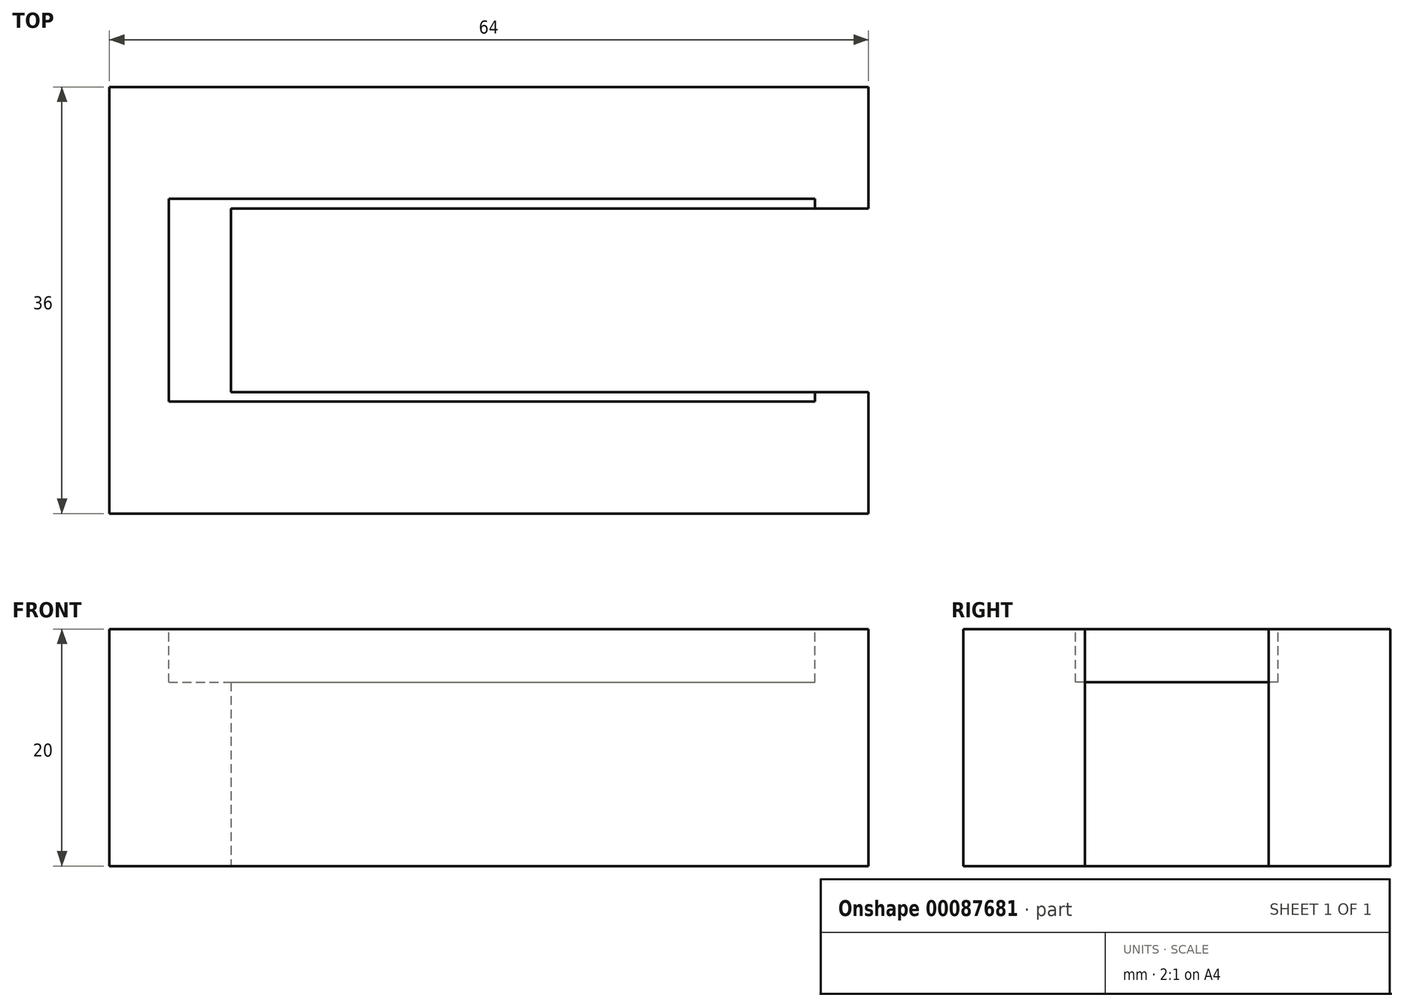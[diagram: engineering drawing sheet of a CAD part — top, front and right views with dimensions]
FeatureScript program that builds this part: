
annotation { "Feature Type Name" : "Feature", "Feature Type Description" : "" }
export const myFeature = defineFeature(function(context is Context, id is Id, definition is map)
    precondition{}
    {
        {
            var Q0;
            Q0=qCreatedBy(makeId("Top.planeOp"),FACE);
            var sketch = newSketch(context, id + "F0", { "sketchPlane" : qUnion([Q0])});
            skLineSegment(sketch, "E0", {"start": v(53.75, 0) * mm, "end": v(-10.25, 0) * mm});
            skLineSegment(sketch, "E1", {"start": v(-10.25, 0) * mm, "end": v(-10.25, 36) * mm});
            skLineSegment(sketch, "E2", {"start": v(-10.25, 36) * mm, "end": v(53.75, 36) * mm});
            skLineSegment(sketch, "E3", {"start": v(53.75, 36) * mm, "end": v(53.75, 25.75) * mm});
            skLineSegment(sketch, "E4", {"start": v(53.75, 25.75) * mm, "end": v(0, 25.75) * mm});
            skLineSegment(sketch, "E5", {"start": v(0, 25.75) * mm, "end": v(0, 10.25) * mm});
            skLineSegment(sketch, "E6", {"start": v(0, 10.25) * mm, "end": v(53.75, 10.25) * mm});
            skLineSegment(sketch, "E7", {"start": v(53.75, 10.25) * mm, "end": v(53.75, 0) * mm});
            skSolve(sketch);
        }
        {
            var Q0;
            Q0=makeQuery(id+"F0.imprint","IMPRINT",FACE,{"disambiguationData":[TD([[makeQuery(id+"F0.imprint","IMPRINT",EDGE,{"derivedFrom":sQuery(id+"F0.wireOp",EDGE,"E0")}),-1.0]])]});
            extrude(context, id + "F1", {"entities" : qUnion([Q0]), "depth" : 20 * mm});
        }
        {
            var Q0;
            Q0=makeQuery(id+"F1.opExtrude","CAP_FACE",FACE,{"disambiguationData":[OSD([sQuery(id+"F0.wireOp",EDGE,"E0"),sQuery(id+"F0.wireOp",EDGE,"E1"),sQuery(id+"F0.wireOp",EDGE,"E2"),sQuery(id+"F0.wireOp",EDGE,"E3"),sQuery(id+"F0.wireOp",EDGE,"E4"),sQuery(id+"F0.wireOp",EDGE,"E5"),sQuery(id+"F0.wireOp",EDGE,"E6"),sQuery(id+"F0.wireOp",EDGE,"E7")])],"isStart":false});
            var sketch = newSketch(context, id + "F2", { "sketchPlane" : qUnion([Q0])});
            skLineSegment(sketch, "E8.bottom", {"start": v(-5.25, 26.55) * mm, "end": v(49.25, 26.55) * mm});
            skLineSegment(sketch, "E8.top", {"start": v(-5.25, 9.45) * mm, "end": v(49.25, 9.45) * mm});
            skLineSegment(sketch, "E8.left", {"start": v(-5.25, 26.55) * mm, "end": v(-5.25, 9.45) * mm});
            skLineSegment(sketch, "E8.right", {"start": v(49.25, 26.55) * mm, "end": v(49.25, 9.45) * mm});
            skSolve(sketch);
        }
        {
            var Q0;
            {var subQ1=sQuery(id+"F2.wireOp",EDGE,"E8.bottom");Q0=makeQuery(id+"F2.imprint","IMPRINT",FACE,{"disambiguationData":[TD([[makeQuery(id+"F2.imprint","IMPRINT",EDGE,{"derivedFrom":subQ1}),-1.0]])]});}
            extrude(context, id + "F3", {"entities" : qUnion([Q0]), "operationType" : NewBodyOperationType.REMOVE, "oppositeDirection" : true, "depth" : 4.5 * mm});
        }
    });
